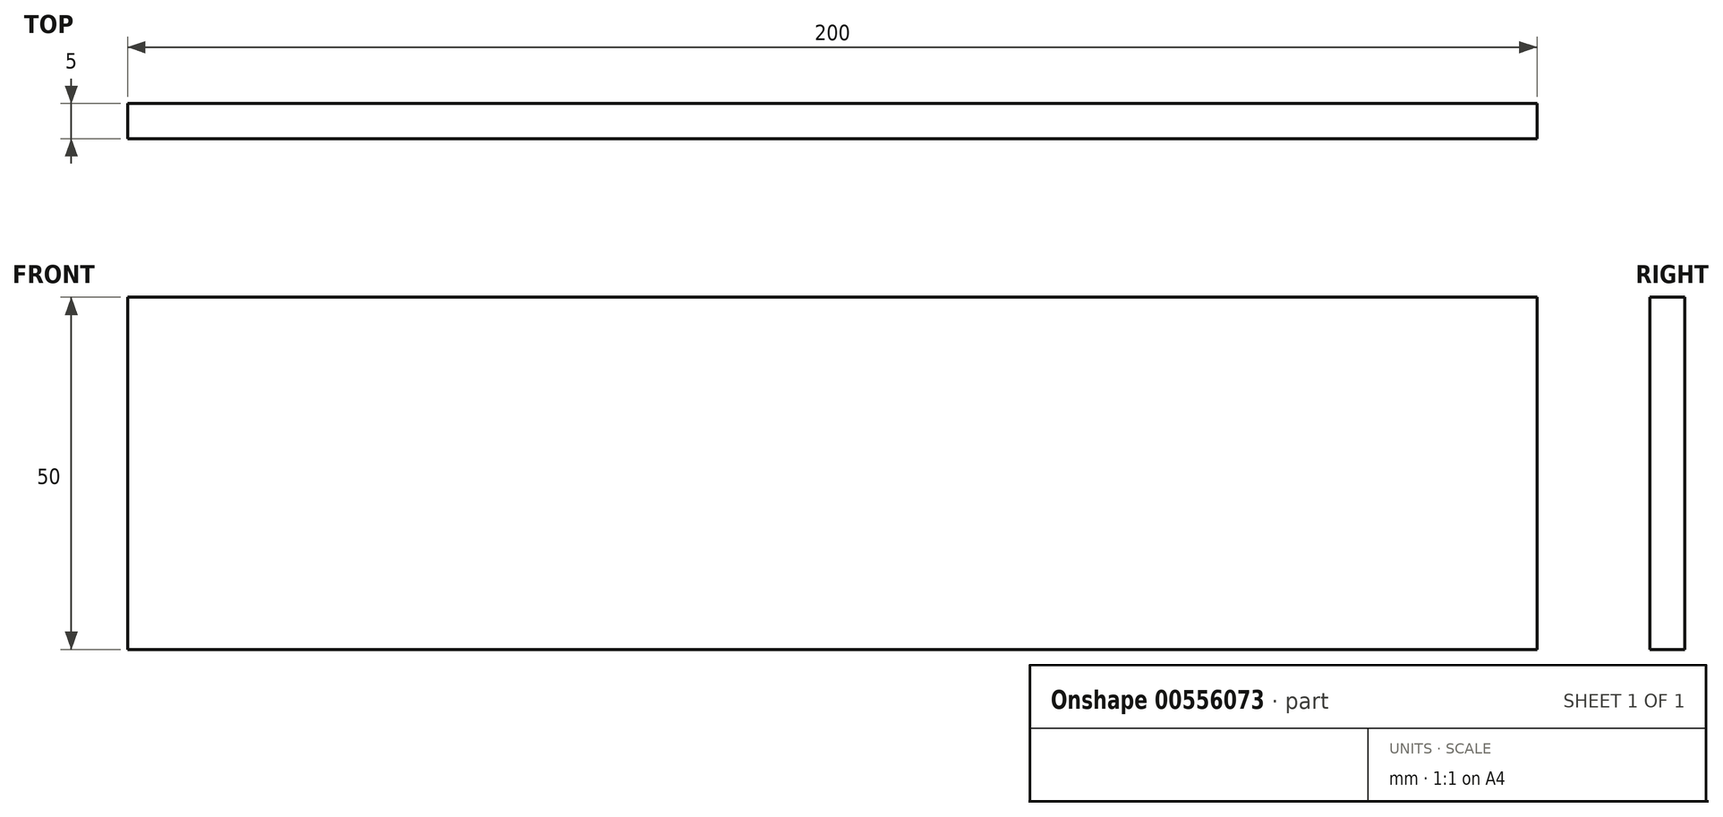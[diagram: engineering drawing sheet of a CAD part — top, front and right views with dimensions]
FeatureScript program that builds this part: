
annotation { "Feature Type Name" : "Feature", "Feature Type Description" : "" }
export const myFeature = defineFeature(function(context is Context, id is Id, definition is map)
    precondition{}
    {
        {
            var Q0;
            Q0=qCreatedBy(makeId("Front.planeOp"),FACE);
            var sketch = newSketch(context, id + "F0", { "sketchPlane" : qUnion([Q0])});
            skLineSegment(sketch, "E0.bottom", {"start": v(-90.65, -5.2) * mm, "end": v(109.35, -5.2) * mm});
            skLineSegment(sketch, "E0.top", {"start": v(-90.65, -55.2) * mm, "end": v(109.35, -55.2) * mm});
            skLineSegment(sketch, "E0.left", {"start": v(-90.65, -5.2) * mm, "end": v(-90.65, -55.2) * mm});
            skLineSegment(sketch, "E0.right", {"start": v(109.35, -5.2) * mm, "end": v(109.35, -55.2) * mm});
            skSolve(sketch);
        }
        {
            var Q0;
            Q0=makeQuery(id+"F0.imprint","IMPRINT",FACE,{"disambiguationData":[TD([[makeQuery(id+"F0.imprint","IMPRINT",EDGE,{"derivedFrom":sQuery(id+"F0.wireOp",EDGE,"E0.bottom")}),-1.0]])]});
            extrude(context, id + "F1", {"entities" : qUnion([Q0]), "depth" : 5 * mm, "offsetDistance" : 25 * mm});
        }
    });
